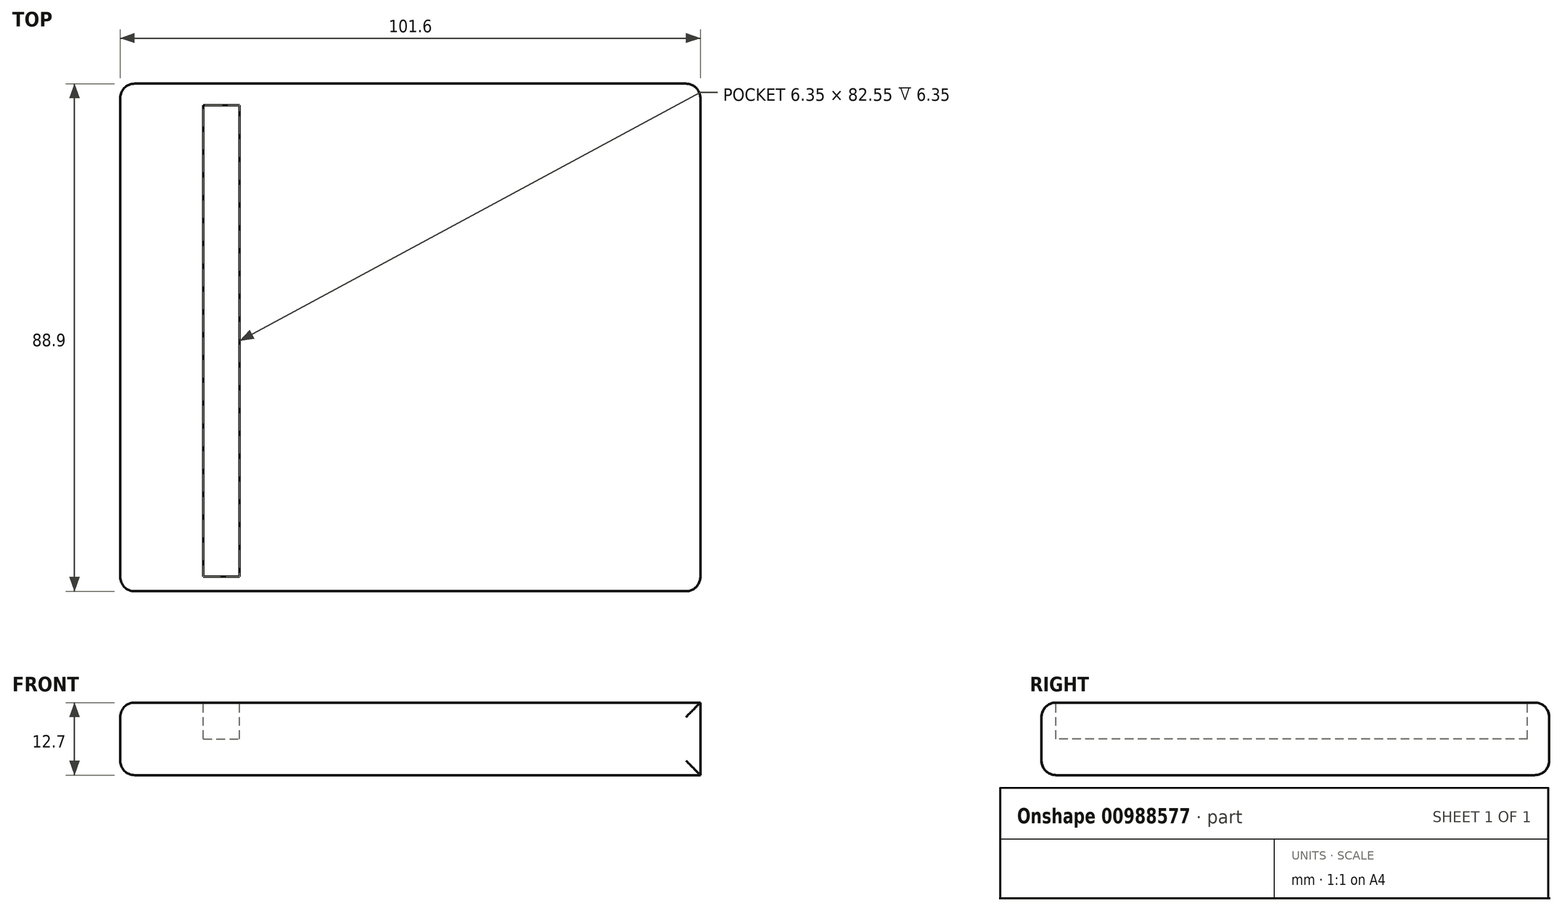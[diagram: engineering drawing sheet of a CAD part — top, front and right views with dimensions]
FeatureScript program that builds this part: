
annotation { "Feature Type Name" : "Feature", "Feature Type Description" : "" }
export const myFeature = defineFeature(function(context is Context, id is Id, definition is map)
    precondition{}
    {
        {
            var Q0;
            Q0=qCreatedBy(makeId("Top.planeOp"),FACE);
            var sketch = newSketch(context, id + "F0", { "sketchPlane" : qUnion([Q0])});
            skLineSegment(sketch, "E0.bottom", {"start": v(-58.78, -42.02) * mm, "end": v(42.82, -42.02) * mm});
            skLineSegment(sketch, "E0.top", {"start": v(-58.78, 46.88) * mm, "end": v(42.82, 46.88) * mm});
            skLineSegment(sketch, "E0.left", {"start": v(-58.78, -42.02) * mm, "end": v(-58.78, 46.88) * mm});
            skLineSegment(sketch, "E0.right", {"start": v(42.82, -42.02) * mm, "end": v(42.82, 46.88) * mm});
            skLineSegment(sketch, "E1.bottom", {"start": v(42.82, 46.88) * mm, "end": v(42.82, 46.88) * mm});
            skLineSegment(sketch, "E1.top", {"start": v(42.82, -42.02) * mm, "end": v(42.82, -42.02) * mm});
            skLineSegment(sketch, "E1.left", {"start": v(42.82, 46.88) * mm, "end": v(42.82, -42.02) * mm});
            skLineSegment(sketch, "E1.right", {"start": v(42.82, 46.88) * mm, "end": v(42.82, -42.02) * mm});
            skCircle(sketch, "E2", {"center": v(0, 0) * mm, "radius": 6.35 * mm});
            skSolve(sketch);
        }
        {
            var Q0;
            Q0=makeQuery(id+"F0.imprint","IMPRINT",FACE,{"disambiguationData":[TD([[makeQuery(id+"F0.imprint","IMPRINT",EDGE,{"derivedFrom":sQuery(id+"F0.wireOp",EDGE,"E0.bottom")}),1.0]])]});
            extrude(context, id + "F1", {"entities" : qUnion([Q0]), "oppositeDirection" : true, "depth" : 12.7 * mm, "offsetDistance" : 25.4 * mm});
        }
        {
            var Q0;
            Q0=makeQuery(id+"F1.opExtrude","CAP_EDGE",EDGE,{"disambiguationData":[OSD([sQuery(id+"F0.wireOp",EDGE,"E0.left")])],"isStart":true});
            var Q1;
            Q1=makeQuery(id+"F1.opExtrude","CAP_EDGE",EDGE,{"disambiguationData":[OSD([sQuery(id+"F0.wireOp",EDGE,"E0.bottom")])],"isStart":true});
            var Q2;
            Q2=makeQuery(id+"F1.opExtrude","CAP_EDGE",EDGE,{"disambiguationData":[OSD([sQuery(id+"F0.wireOp",EDGE,"E0.top")])],"isStart":true});
            var Q3;
            Q3=makeQuery(id+"F1.opExtrude","CAP_EDGE",EDGE,{"disambiguationData":[OSD([sQuery(id+"F0.wireOp",EDGE,"E1.right")])],"isStart":true});
            var Q4;
            Q4=makeQuery(id+"F1.opExtrude","CAP_EDGE",EDGE,{"disambiguationData":[OSD([sQuery(id+"F0.wireOp",EDGE,"E0.bottom")])],"isStart":false});
            var Q5;
            Q5=makeQuery(id+"F1.opExtrude","SWEPT_EDGE",EDGE,{"disambiguationData":[OSD([sQuery(id+"F0.wireOp",EDGE,"E0.bottom"),sQuery(id+"F0.wireOp",EDGE,"E0.left")])]});
            var Q6;
            Q6=makeQuery(id+"F1.opExtrude","SWEPT_EDGE",EDGE,{"disambiguationData":[OSD([sQuery(id+"F0.wireOp",EDGE,"E0.bottom"),sQuery(id+"F0.wireOp",EDGE,"E1.right")])]});
            var Q7;
            Q7=makeQuery(id+"F1.opExtrude","CAP_EDGE",EDGE,{"disambiguationData":[OSD([sQuery(id+"F0.wireOp",EDGE,"E1.right")])],"isStart":false});
            var Q8;
            Q8=makeQuery(id+"F1.opExtrude","SWEPT_EDGE",EDGE,{"disambiguationData":[OSD([sQuery(id+"F0.wireOp",EDGE,"E0.top"),sQuery(id+"F0.wireOp",EDGE,"E1.right")])]});
            var Q9;
            Q9=makeQuery(id+"F1.opExtrude","CAP_EDGE",EDGE,{"disambiguationData":[OSD([sQuery(id+"F0.wireOp",EDGE,"E0.top")])],"isStart":false});
            var Q10;
            Q10=makeQuery(id+"F1.opExtrude","SWEPT_EDGE",EDGE,{"disambiguationData":[OSD([sQuery(id+"F0.wireOp",EDGE,"E0.top"),sQuery(id+"F0.wireOp",EDGE,"E0.left")])]});
            var Q11;
            Q11=makeQuery(id+"F1.opExtrude","CAP_EDGE",EDGE,{"disambiguationData":[OSD([sQuery(id+"F0.wireOp",EDGE,"E0.left")])],"isStart":false});
            fillet(context, id + "F2", {"entities" : qUnion([Q0, Q1, Q2, Q3, Q4, Q5, Q6, Q7, Q8, Q9, Q10, Q11]), "radius" : 2.54 * mm, "tangentPropagation" : true, "allowEdgeOverflow" : false});
        }
        {
            var Q0;
            Q0=makeQuery(id+"F0.imprint","IMPRINT",FACE,{"disambiguationData":[TD([[makeQuery(id+"F0.imprint","IMPRINT",EDGE,{"derivedFrom":sQuery(id+"F0.wireOp",EDGE,"E2")}),1.0]])]});
            extrude(context, id + "F3", {"entities" : qUnion([Q0]), "operationType" : NewBodyOperationType.ADD, "oppositeDirection" : true, "depth" : 12.7 * mm, "offsetDistance" : 25.4 * mm});
        }
        {
            var Q0;
            {var subQ0=sQuery(id+"F0.wireOp",EDGE,"E2");Q0=makeQuery(id+"F3.boolean.opBoolean","MERGE",FACE,{"derivedFrom":[makeQuery(id+"F1.opExtrude","CAP_FACE",FACE,{"disambiguationData":[OSD([sQuery(id+"F0.wireOp",EDGE,"E0.bottom"),sQuery(id+"F0.wireOp",EDGE,"E0.top"),sQuery(id+"F0.wireOp",EDGE,"E0.left"),sQuery(id+"F0.wireOp",EDGE,"E1.right"),subQ0])],"isStart":true}),makeQuery(id+"F3.opExtrude","CAP_FACE",FACE,{"disambiguationData":[OSD([subQ0])],"isStart":true})]});}
            var sketch = newSketch(context, id + "F4", { "sketchPlane" : qUnion([Q0])});
            skLineSegment(sketch, "E3.bottom", {"start": v(-44.22, 43.07) * mm, "end": v(-37.87, 43.07) * mm});
            skLineSegment(sketch, "E3.top", {"start": v(-44.22, -39.48) * mm, "end": v(-37.87, -39.48) * mm});
            skLineSegment(sketch, "E3.left", {"start": v(-44.22, 43.07) * mm, "end": v(-44.22, -39.48) * mm});
            skLineSegment(sketch, "E3.right", {"start": v(-37.87, 43.07) * mm, "end": v(-37.87, -39.48) * mm});
            skSolve(sketch);
        }
        {
            var Q0;
            Q0=makeQuery(id+"F4.imprint","IMPRINT",FACE,{"disambiguationData":[TD([[makeQuery(id+"F4.imprint","IMPRINT",EDGE,{"derivedFrom":sQuery(id+"F4.wireOp",EDGE,"E3.bottom")}),-1.0]])]});
            extrude(context, id + "F5", {"entities" : qUnion([Q0]), "operationType" : NewBodyOperationType.REMOVE, "oppositeDirection" : true, "depth" : 6.35 * mm, "offsetDistance" : 25.4 * mm});
        }
    });
